# Revit family: IPSOS
name_source: partatom
category: Plumbing Fixtures
revit_build: Autodesk Revit 2017 (Build: 20160225_1515(x64)
units: mm (PartAtom-declared; Revit-internal decimal feet)

## family parameters
Always vertical = Yes
Cut with Voids When Loaded = No
OmniClass Number = 23.45.00.00
OmniClass Title = Sanitary, Laundry, and Cleaning Equipment
Part Type = Normal
Room Calculation Point = No
Round Connector Dimension = Use Diameter
Shared = No
Work Plane-Based = No

## types (2) — shared parameters
Chrome = CHROME
Manufacturer = SEIMA
Model = IPSOS
URL = www.seima.com.au
Waste size = 32 mm  [stored 0.104987 ft]

## per-type parameters (varying)
| type | Basin Meterial |
| IPSOS_White | Vitreous china_White |
| IPSOS_Black | Vitreous china_Soft black |

note: [stored X ft] marks values corroborated as IEEE doubles in the binary element streams (Revit-internal decimal feet)

## geometry (parser evidence)
native form markers: Sweep x2
no freeform markers — native parametric forms only
